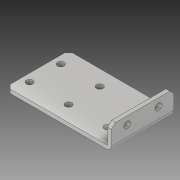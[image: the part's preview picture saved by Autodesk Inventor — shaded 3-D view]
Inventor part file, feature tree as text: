
AUTODESK INVENTOR PART (.ipt)
format: ipt  version: 2018 (Build 220112000, 112)  size: 127,488 bytes
history: native  units: in
note: dims shown in document units (in); Inventor stores cm internally (conversion verified against a paired STEP export)
features: chamfer x1
ambient origin geometry x8: Origin, YZ Plane, XZ Plane, XY Plane, X Axis, Y Axis, Z Axis, Center Point
bodies: Solid1 (feature_tree)
feature tree (1):
  chamfer  "Chamfer2"  [1 undecoded]
note: 1 required parameter value undecoded (feature->parameter linkage not recoverable at this tier; creation-order binding heuristic only, values carry confidence <= 0.55)
